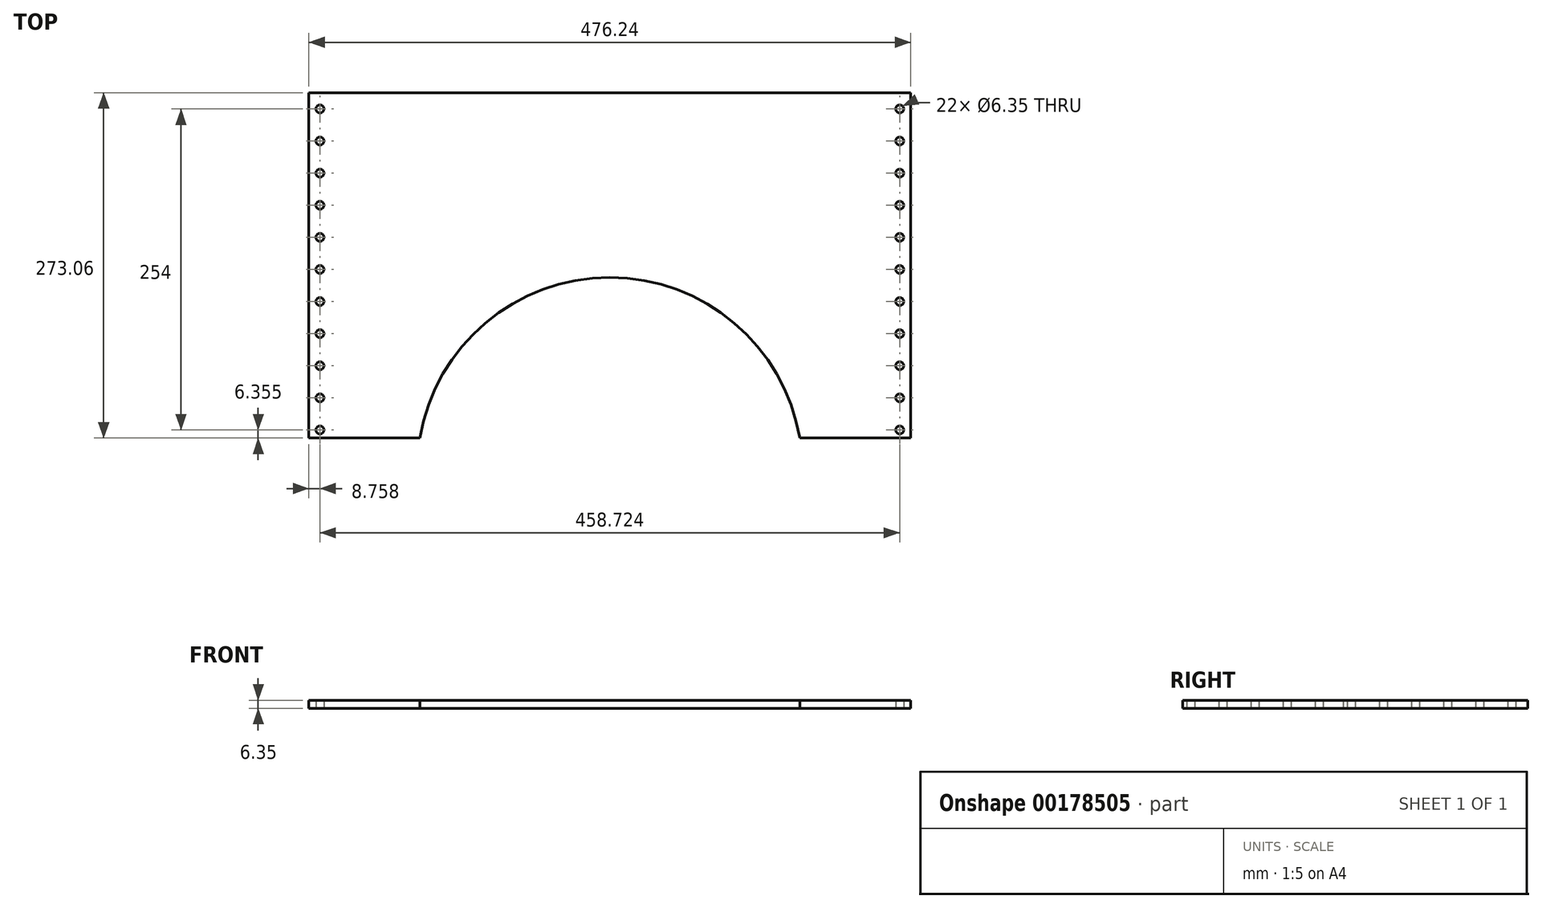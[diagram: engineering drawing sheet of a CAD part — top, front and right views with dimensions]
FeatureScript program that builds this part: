
annotation { "Feature Type Name" : "Feature", "Feature Type Description" : "" }
export const myFeature = defineFeature(function(context is Context, id is Id, definition is map)
    precondition{}
    {
        {
            var Q0;
            Q0=qCreatedBy(makeId("Top.planeOp"),FACE);
            var sketch = newSketch(context, id + "F0", { "sketchPlane" : qUnion([Q0])});
            skLineSegment(sketch, "E0.bottom", {"start": v(-238.12, 136.52) * mm, "end": v(238.12, 136.52) * mm});
            skLineSegment(sketch, "E0.top", {"start": v(-238.12, -136.53) * mm, "end": v(238.12, -136.53) * mm});
            skLineSegment(sketch, "E0.left", {"start": v(-238.12, 136.53) * mm, "end": v(-238.12, -136.53) * mm});
            skLineSegment(sketch, "E0.right", {"start": v(238.13, 136.53) * mm, "end": v(238.13, -136.53) * mm});
            skPoint(sketch, "E0.middle", {"position": v(0, 0) * mm});
            skLineSegment(sketch, "E1", {"start": v(0, -136.53) * mm, "end": v(0, -161.93) * mm});
            skPoint(sketch, "E1.endSnap0", {"position": v(0, -136.53) * mm});
            skCircle(sketch, "E2", {"center": v(0, -161.93) * mm, "radius": 152.4 * mm});
            skCircle(sketch, "E3", {"center": v(229.36, -130.18) * mm, "radius": 3.18 * mm});
            skPoint(sketch, "E4", {"position": v(223.01, -136.53) * mm});
            skLineSegment(sketch, "E5", {"start": v(223.01, -136.53) * mm, "end": v(223.01, 136.53) * mm});
            skCircle(sketch, "E6.0.1.0", {"center": v(229.36, -104.78) * mm, "radius": 3.18 * mm});
            skCircle(sketch, "E6.0.2.0", {"center": v(229.36, -79.38) * mm, "radius": 3.18 * mm});
            skCircle(sketch, "E6.0.3.0", {"center": v(229.36, -53.98) * mm, "radius": 3.18 * mm});
            skCircle(sketch, "E6.0.4.0", {"center": v(229.36, -28.58) * mm, "radius": 3.18 * mm});
            skCircle(sketch, "E6.0.5.0", {"center": v(229.36, -3.18) * mm, "radius": 3.18 * mm});
            skCircle(sketch, "E6.0.6.0", {"center": v(229.36, 22.22) * mm, "radius": 3.18 * mm});
            skCircle(sketch, "E6.0.7.0", {"center": v(229.36, 47.62) * mm, "radius": 3.18 * mm});
            skCircle(sketch, "E6.0.8.0", {"center": v(229.36, 73.02) * mm, "radius": 3.18 * mm});
            skCircle(sketch, "E6.0.9.0", {"center": v(229.36, 98.42) * mm, "radius": 3.18 * mm});
            skCircle(sketch, "E6.0.10.0", {"center": v(229.36, 123.82) * mm, "radius": 3.18 * mm});
            skLineSegment(sketch, "E6.direction1", {"start": v(229.36, -130.18) * mm, "end": v(254.76, -130.18) * mm, "construction": true});
            skLineSegment(sketch, "E6.direction2", {"start": v(229.36, -130.18) * mm, "end": v(229.36, -104.78) * mm, "construction": true});
            skCircle(sketch, "E7.MirrorC", {"center": v(-229.36, 98.42) * mm, "radius": 3.18 * mm});
            skCircle(sketch, "E8.MirrorC", {"center": v(-229.36, 123.82) * mm, "radius": 3.18 * mm});
            skCircle(sketch, "E9.MirrorC", {"center": v(-229.36, 73.02) * mm, "radius": 3.18 * mm});
            skCircle(sketch, "E10.MirrorC", {"center": v(-229.36, 47.62) * mm, "radius": 3.18 * mm});
            skCircle(sketch, "E11.MirrorC", {"center": v(-229.36, -3.18) * mm, "radius": 3.18 * mm});
            skCircle(sketch, "E12.MirrorC", {"center": v(-229.36, -28.58) * mm, "radius": 3.18 * mm});
            skCircle(sketch, "E13.MirrorC", {"center": v(-229.36, -53.98) * mm, "radius": 3.18 * mm});
            skCircle(sketch, "E14.MirrorC", {"center": v(-229.36, -79.38) * mm, "radius": 3.18 * mm});
            skCircle(sketch, "E15.MirrorC", {"center": v(-229.36, -104.78) * mm, "radius": 3.18 * mm});
            skCircle(sketch, "E16.MirrorC", {"center": v(-229.36, -130.18) * mm, "radius": 3.18 * mm});
            skCircle(sketch, "E17.MirrorC", {"center": v(-229.36, 22.22) * mm, "radius": 3.18 * mm});
            skSolve(sketch);
        }
        {
            var Q0;
            Q0=makeQuery(id+"F0.imprint","IMPRINT",FACE,{"disambiguationData":[TD([[makeQuery(id+"F0.imprint","IMPRINT",EDGE,{"derivedFrom":sQuery(id+"F0.wireOp",EDGE,"E0.bottom")}),-1.0]])]});
            var Q1;
            {var subQ0=sQuery(id+"F0.wireOp",EDGE,"E0.left");Q1=makeQuery(id+"F0.imprint","IMPRINT",FACE,{"disambiguationData":[TD([[makeQuery(id+"F0.imprint","IMPRINT",EDGE,{"derivedFrom":subQ0}),1.0]])]});}
            extrude(context, id + "F1", {"entities" : qUnion([Q0, Q1]), "depth" : 6.35 * mm});
        }
    });
